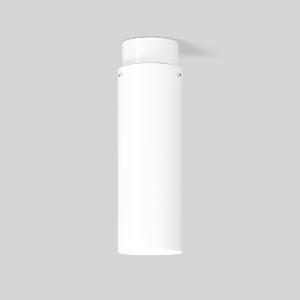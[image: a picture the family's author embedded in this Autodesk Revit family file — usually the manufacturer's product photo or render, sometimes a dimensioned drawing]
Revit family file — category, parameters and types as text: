
# Revit family: glasdownlight_931180_002_1_76_cfd9
name_source: partatom
category: Lighting Fixtures
units: mm (PartAtom-declared; Revit-internal decimal feet)

## family parameters
Cut with Voids When Loaded = No
Host = Face
Light Source = No
Part Type = Normal
Room Calculation Point = No
Round Connector Dimension = Use Diameter
Shared = No

## types (1)
- GLASDOWNLIGHT (1 x LED Modul 840, 3550 lm, 4000)
    Apparent Load = 26 VA
    CIE Flux Codes = 24 49 74 56 100
    Color Rendering = 80
    Color Temperature = 4000
    Default Elevation = 1800 mm
    Description = Series: GLASDOWNLIGHT
Decorative round surface-mounted luminaire. Base: aluminium, powder-coated. Mouth blown 3-layer opal glass (Triplex glass) with satin finish. Glass fastening: retaining screws. Triplex glass produces particularly homogeneous, soft and glare free lighting. 
Colour: white
Diameter: 150 mm
Height: 470 mm
Lamp: LED
Socket: without socket
Colour temperature: 4000K
Colour rendering index (CRI): 80
System power: 26 W
Rated luminous flux: 3550 lm
Luminous efficiency: 137 lm/W
Control gear: Converter, dimmable, DALI
Protection class: I
Type of protection: IP 20
    Height = 470 mm
    Lamp = 1 x LED Modul 840
    Lamp Light Flux = 3550 lm
    Lamp count = 1
    Length = 150 mm
    Lifetime = 50000 h
    Luminous efficacy = 137 lm/W
    Manufacturer = RZB
    ModVariant = No
    Model = 931180.002.1.76
    Mounting Place = Ceiling
    Mounting Type = Surface mounted
    Number of Poles = 1
    OnlyDefault = Yes
    Power Factor = 1
    Product Name = GLASDOWNLIGHT
    Product group = Surface mounted ceiling luminaires
    ProductGroupID = 303
    Protection Class = Protection class I
    Protection Degree = IP 20
    RLX_Detail_Level = 1
    RLX_Emergency_Light_Flux = 0 lm
    RLX_Emergency_Type = 0
    RLX_Emergency_Type_DB = No
    RlxData = <blob elided: 15485 chars, md5=28a8b64a>
    Socket = socket
    Standby Power = 0 W
    System Light Flux = 3550 lm
    System Power = 26 W
    Type Comments = Product without accessories
    Type Image = 931180.002.jpg
    URL = http://relux.com
    VarID = ---
    Voltage = 230 V
    Voltage Range = 220-240 V
    Weight = 0.00 kg
    Width = 0 mm  [stored 0 ft]

note: [stored X ft] marks values corroborated as IEEE doubles in the binary element streams (Revit-internal decimal feet)

## geometry (parser evidence)
native form markers: Sweep x14
no freeform markers — native parametric forms only
